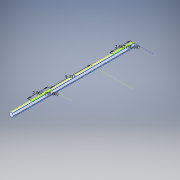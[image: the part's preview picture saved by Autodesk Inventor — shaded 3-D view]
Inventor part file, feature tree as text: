
AUTODESK INVENTOR PART (.ipt)
format: ipt  version: 2017 (Build 210142000, 142)  size: 148,992 bytes
history: native  units: in
note: dims shown in document units (in); Inventor stores cm internally (conversion verified against a paired STEP export)
features: sketch x5, split x1, fillet x1
ambient origin geometry x8: Origin, YZ Plane, XZ Plane, XY Plane, X Axis, Y Axis, Z Axis, Center Point
bodies: Solid1 (feature_tree)
feature tree (7):
  sketch  "Sketch1"  dims[d3=8.5in]
  split  "Split1"
  sketch  "Sketch3"  dims[d7=2.6665in]
  sketch  "Sketch4"  dims[d8=90.0deg]
  sketch  "Sketch5"  dims[d9=2.6665in d10=90.0deg]
  sketch  "Sketch2"  dims[d5=5.333in]
  fillet  "Fillet1"  Radius=16.0in
